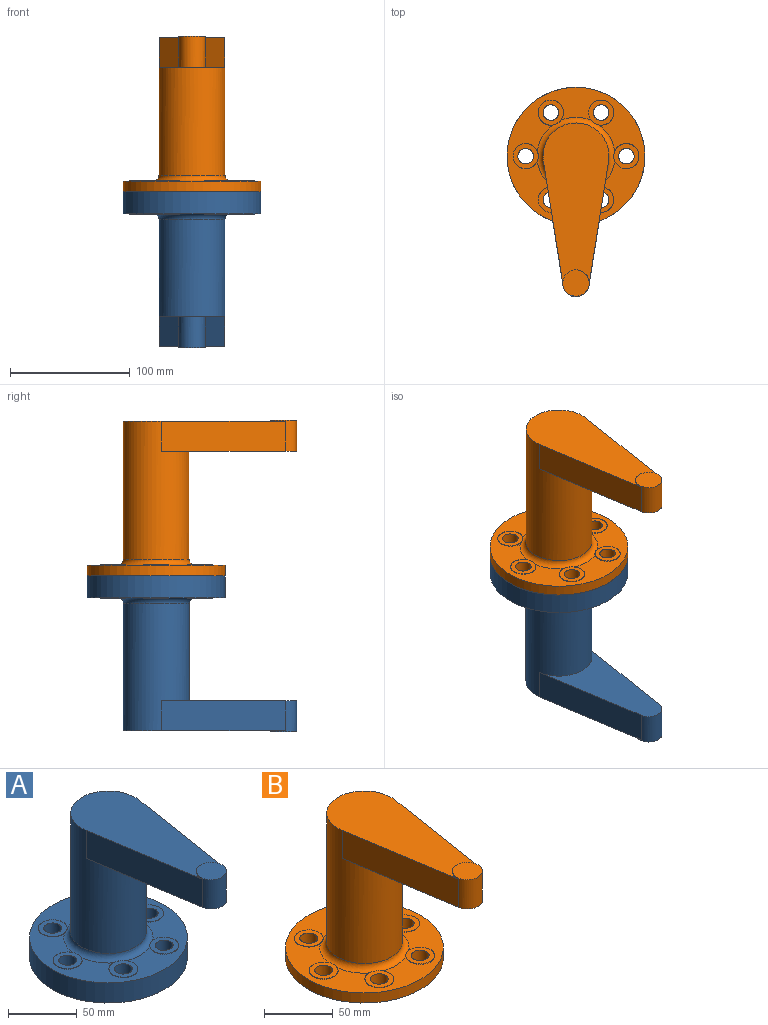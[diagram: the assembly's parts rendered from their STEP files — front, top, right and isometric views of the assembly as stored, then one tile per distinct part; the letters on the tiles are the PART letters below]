
ASSEMBLY  parts=2 mates=1
PART A: 31 faces, bbox 115x174.5x130 mm
  f0: plane 115x115mm, normal (0,0,1), area 5022mm2, adj f4,f5,f6,f9,f12,f15,f18,f21
  f1: cylinder r=27.5mm len=106mm, axis (0,0,-1), area 16370.5mm2, adj f5,f24,f25,f26,f27
  f2: cylinder r=12.5mm len=104mm, axis (0,0,-1), area 8168.1mm2, adj f3,f29
  f3: plane 115x115mm, normal (0,0,-1), area 9099.6mm2, adj f2,f4,f7,f10,f13,f16,f19,f22
  f4: cylinder r=57.5mm len=115mm, axis (0,0,-1), area 6503.1mm2, adj f0,f3
  f5: torus R=32.5mm, axis (0,0,-1), area 1415mm2, adj f0,f1,f6,f9,f12,f15,f18,f21
  f6: cylinder r=10.5mm len=21mm, axis (0,0,-1), area 32.6mm2, adj f0,f5,f8
  f7: cylinder r=6.5mm len=18.5mm, axis (0,0,-1), area 755.6mm2, adj f3,f8
  f8: plane 21x21mm, normal (0,0,1), area 213.6mm2, adj f6,f7
  f9: cylinder r=10.5mm len=21mm, axis (0,0,-1), area 32.6mm2, adj f0,f5,f11
  f10: cylinder r=6.5mm len=18.5mm, axis (0,0,-1), area 755.6mm2, adj f3,f11
  f11: plane 21x21mm, normal (0,0,1), area 213.6mm2, adj f9,f10
  f12: cylinder r=10.5mm len=21mm, axis (0,0,-1), area 32.6mm2, adj f0,f5,f14
  f13: cylinder r=6.5mm len=18.5mm, axis (0,0,-1), area 755.6mm2, adj f3,f14
  f14: plane 21x21mm, normal (0,0,1), area 213.6mm2, adj f12,f13
  f15: cylinder r=10.5mm len=21mm, axis (0,0,-1), area 32.6mm2, adj f0,f5,f17
  f16: cylinder r=6.5mm len=18.5mm, axis (0,0,-1), area 755.6mm2, adj f3,f17
  f17: plane 21x21mm, normal (0,0,1), area 213.6mm2, adj f15,f16
  f18: cylinder r=10.5mm len=21mm, axis (0,0,-1), area 32.6mm2, adj f0,f5,f20
  f19: cylinder r=6.5mm len=18.5mm, axis (0,0,-1), area 755.6mm2, adj f3,f20
  f20: plane 21x21mm, normal (0,0,1), area 213.6mm2, adj f18,f19
  f21: cylinder r=10.5mm len=21mm, axis (0,0,-1), area 32.6mm2, adj f0,f5,f23
  f22: cylinder r=6.5mm len=18.5mm, axis (0,0,-1), area 755.6mm2, adj f3,f23
  f23: plane 21x21mm, normal (0,0,1), area 213.6mm2, adj f21,f22
  f24: plane 112.72x54.33mm, normal (0,0,-1), area 3132.7mm2, adj f1,f26,f27,f28
  f25: plane 135.21x55mm, normal (0,0,1), area 5128.4mm2, adj f1,f26,f27,f28
  f26: plane 103.43x25mm, normal (-0.99,-0.16,0), area 2617.7mm2, adj f1,f24,f25,f28
  f27: plane 103.43x25mm, normal (0.99,-0.16,0), area 2617.7mm2, adj f1,f24,f25,f28
  f28: cylinder r=11mm len=26mm, axis (0,0,-1), area 847.1mm2, adj f24,f25,f26,f27,f30
  f29: plane 25x25mm, normal (0,0,-1), area 490.9mm2, adj f2
  f30: plane 22x22mm, normal (0,0,1), area 380.1mm2, adj f28
PART B: 31 faces, bbox 115x174.5x130 mm
  f0: plane 115x115mm, normal (0,0,1), area 5022mm2, adj f4,f5,f6,f9,f12,f15,f18,f21
  f1: cylinder r=27.5mm len=115mm, axis (0,0,-1), area 17925.6mm2, adj f5,f24,f25,f26,f27
  f2: cylinder r=12.5mm len=104mm, axis (0,0,-1), area 8168.1mm2, adj f3,f29
  f3: plane 115x115mm, normal (0,0,-1), area 9099.6mm2, adj f2,f4,f7,f10,f13,f16,f19,f22
  f4: cylinder r=57.5mm len=115mm, axis (0,0,-1), area 3251.5mm2, adj f0,f3
  f5: torus R=32.5mm, axis (0,0,-1), area 1415mm2, adj f0,f1,f6,f9,f12,f15,f18,f21
  f6: cylinder r=10.5mm len=21mm, axis (0,0,-1), area 32.6mm2, adj f0,f5,f8
  f7: cylinder r=6.5mm len=13mm, axis (0,0,-1), area 388mm2, adj f3,f8
  f8: plane 21x21mm, normal (0,0,1), area 213.6mm2, adj f6,f7
  f9: cylinder r=10.5mm len=21mm, axis (0,0,-1), area 32.6mm2, adj f0,f5,f11
  f10: cylinder r=6.5mm len=13mm, axis (0,0,-1), area 388mm2, adj f3,f11
  f11: plane 21x21mm, normal (0,0,1), area 213.6mm2, adj f9,f10
  f12: cylinder r=10.5mm len=21mm, axis (0,0,-1), area 32.6mm2, adj f0,f5,f14
  f13: cylinder r=6.5mm len=13mm, axis (0,0,-1), area 388mm2, adj f3,f14
  f14: plane 21x21mm, normal (0,0,1), area 213.6mm2, adj f12,f13
  f15: cylinder r=10.5mm len=21mm, axis (0,0,-1), area 32.6mm2, adj f0,f5,f17
  f16: cylinder r=6.5mm len=13mm, axis (0,0,-1), area 388mm2, adj f3,f17
  f17: plane 21x21mm, normal (0,0,1), area 213.6mm2, adj f15,f16
  f18: cylinder r=10.5mm len=21mm, axis (0,0,-1), area 32.6mm2, adj f0,f5,f20
  f19: cylinder r=6.5mm len=13mm, axis (0,0,-1), area 388mm2, adj f3,f20
  f20: plane 21x21mm, normal (0,0,1), area 213.6mm2, adj f18,f19
  f21: cylinder r=10.5mm len=21mm, axis (0,0,-1), area 32.6mm2, adj f0,f5,f23
  f22: cylinder r=6.5mm len=13mm, axis (0,0,-1), area 388mm2, adj f3,f23
  f23: plane 21x21mm, normal (0,0,1), area 213.6mm2, adj f21,f22
  f24: plane 112.72x54.33mm, normal (0,0,-1), area 3132.7mm2, adj f1,f26,f27,f28
  f25: plane 135.21x55mm, normal (0,0,1), area 5128.4mm2, adj f1,f26,f27,f28
  f26: plane 103.43x25mm, normal (-0.99,-0.16,0), area 2617.7mm2, adj f1,f24,f25,f28
  f27: plane 103.43x25mm, normal (0.99,-0.16,0), area 2617.7mm2, adj f1,f24,f25,f28
  f28: cylinder r=11mm len=26mm, axis (0,0,-1), area 847.1mm2, adj f24,f25,f26,f27,f30
  f29: plane 25x25mm, normal (0,0,-1), area 490.9mm2, adj f2
  f30: plane 22x22mm, normal (0,0,1), area 380.1mm2, adj f28
PLACE A rot(axis=(0,1,0),180deg) t=(-25.55,-40.38,10.46)mm
PLACE B t=(-25.55,-40.38,10.46)mm
MATE fastened A.f1 <-> B.f1  axis (0,0,1) through (-25.55,-40.38,10.46)mm
